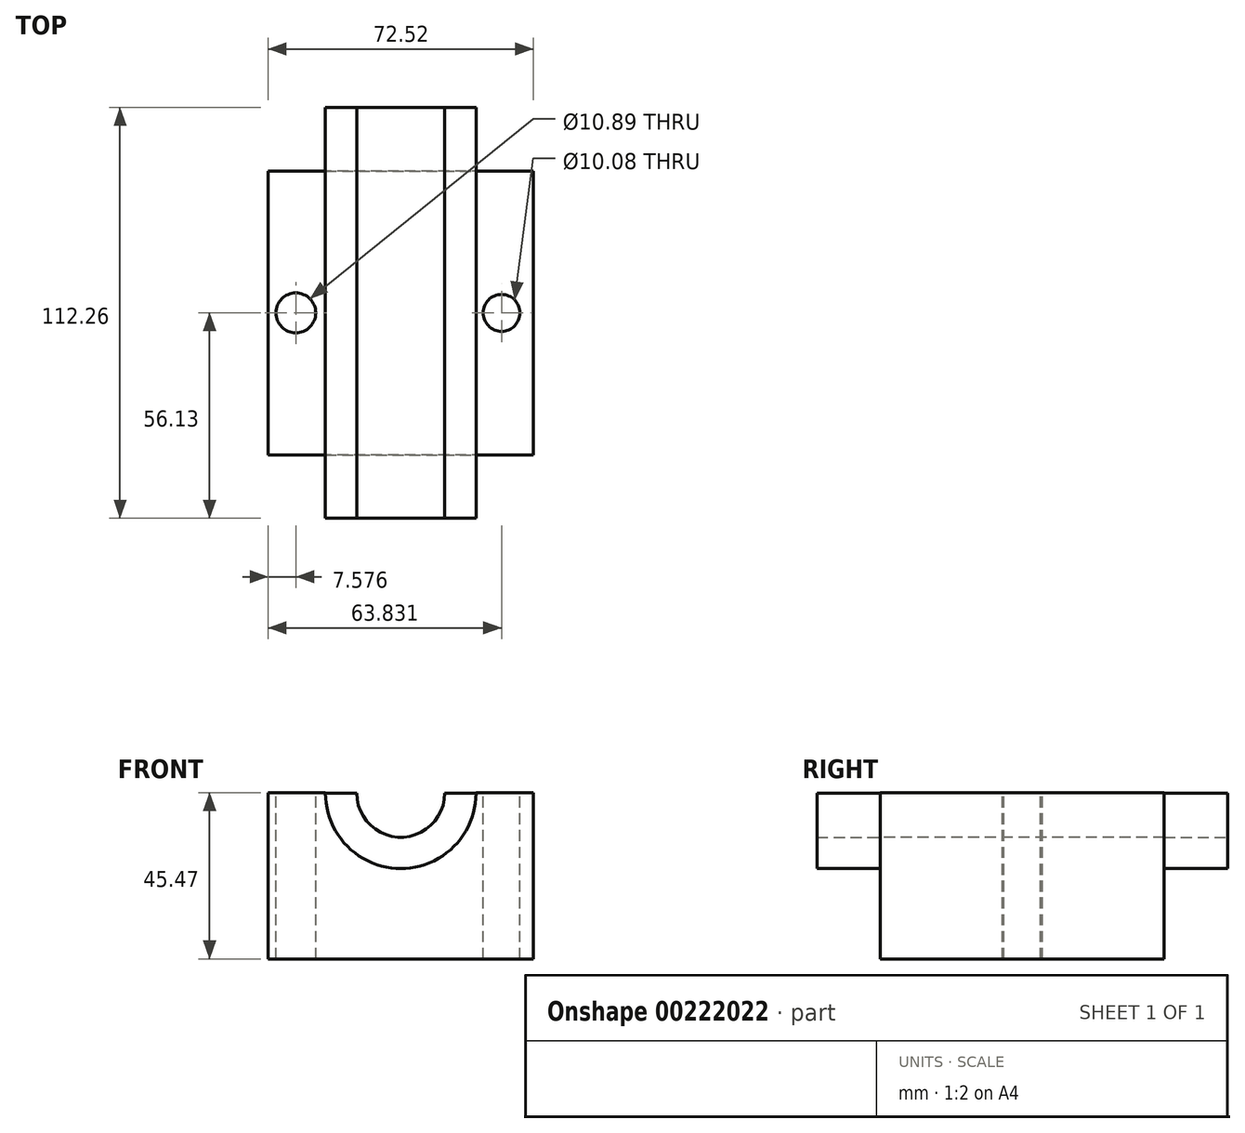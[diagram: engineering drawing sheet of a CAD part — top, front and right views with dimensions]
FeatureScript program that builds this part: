
annotation { "Feature Type Name" : "Feature", "Feature Type Description" : "" }
export const myFeature = defineFeature(function(context is Context, id is Id, definition is map)
    precondition{}
    {
        {
            var Q0;
            Q0=qCreatedBy(makeId("Top.planeOp"),FACE);
            var sketch = newSketch(context, id + "F0", { "sketchPlane" : qUnion([Q0])});
            skLineSegment(sketch, "E0.bottom", {"start": v(36.26, -38.8) * mm, "end": v(-36.26, -38.8) * mm});
            skLineSegment(sketch, "E0.top", {"start": v(36.26, 38.8) * mm, "end": v(-36.26, 38.8) * mm});
            skLineSegment(sketch, "E0.left", {"start": v(36.26, -38.8) * mm, "end": v(36.26, 38.8) * mm});
            skLineSegment(sketch, "E0.right", {"start": v(-36.26, -38.8) * mm, "end": v(-36.26, 38.8) * mm});
            skPoint(sketch, "E0.middle", {"position": v(0, 0) * mm});
            skSolve(sketch);
        }
        {
            var Q0;
            Q0 = qSketchRegion(id + "F0", true);
            extrude(context, id + "F1", {"entities" : qUnion([Q0]), "depth" : 45.47 * mm});
        }
        {
            var Q0;
            Q0=qCreatedBy(makeId("Front.planeOp"),FACE);
            var sketch = newSketch(context, id + "F2", { "sketchPlane" : qUnion([Q0])});
            skCircle(sketch, "E1", {"center": v(0, 45.28) * mm, "radius": 20.59 * mm});
            skCircle(sketch, "E2", {"center": v(0, 45.28) * mm, "radius": 12.02 * mm});
            skSolve(sketch);
        }
        {
            var Q0;
            Q0 = qSketchRegion(id + "F2", true);
            extrude(context, id + "F3", {"entities" : qUnion([Q0]), "operationType" : NewBodyOperationType.ADD, "endBound" : BoundingType.SYMMETRIC, "depth" : 112.27 * mm});
        }
        {
            var Q0;
            Q0=makeQuery(id+"F3.opExtrude","CAP_FACE",FACE,{"disambiguationData":[OSD([sQuery(id+"F2.wireOp",EDGE,"E1"),sQuery(id+"F2.wireOp",EDGE,"E2")])],"isStart":false});
            var sketch = newSketch(context, id + "F4", { "sketchPlane" : qUnion([Q0])});
            skCircle(sketch, "E3", {"center": v(0, 45.28) * mm, "radius": 12.02 * mm});
            skSolve(sketch);
        }
        {
            var Q0;
            Q0 = qSketchRegion(id + "F4", true);
            extrude(context, id + "F5", {"entities" : qUnion([Q0]), "operationType" : NewBodyOperationType.REMOVE, "endBound" : BoundingType.THROUGH_ALL, "oppositeDirection" : true, "depth" : 25.4 * mm});
        }
        {
            var Q0;
            Q0=makeQuery(id+"F3.opExtrude","CAP_FACE",FACE,{"disambiguationData":[OSD([sQuery(id+"F2.wireOp",EDGE,"E1"),sQuery(id+"F2.wireOp",EDGE,"E2")])],"isStart":false});
            var sketch = newSketch(context, id + "F6", { "sketchPlane" : qUnion([Q0])});
            skArc(sketch, "E4", {"start": v(-20.59, 45.3) * mm, "mid": v(0, 65.87) * mm, "end": v(20.59, 45.28) * mm});
            skLineSegment(sketch, "E5", {"start": v(-20.59, 45.3) * mm, "end": v(20.59, 45.28) * mm});
            skSolve(sketch);
        }
        {
            var Q0;
            Q0 = qSketchRegion(id + "F6", true);
            extrude(context, id + "F7", {"entities" : qUnion([Q0]), "operationType" : NewBodyOperationType.REMOVE, "endBound" : BoundingType.THROUGH_ALL, "oppositeDirection" : true, "depth" : 25.4 * mm});
        }
        {
            var Q0;
            {var subQ0=sQuery(id+"F0.wireOp",EDGE,"E0.bottom");var subQ1=sQuery(id+"F0.wireOp",EDGE,"E0.top");var subQ2=sQuery(id+"F0.wireOp",EDGE,"E0.right");Q0=makeQuery(id+"F3.boolean.opBoolean","SPLIT",FACE,{"disambiguationData":[TD([makeQuery(id+"F1.opExtrude","SWEPT_FACE",FACE,{"disambiguationData":[OSD([subQ2])]})])],"derivedFrom":makeQuery(id+"F1.opExtrude","CAP_FACE",FACE,{"disambiguationData":[OSD([subQ0,subQ1,sQuery(id+"F0.wireOp",EDGE,"E0.left"),subQ2])],"isStart":false})});}
            var sketch = newSketch(context, id + "F8", { "sketchPlane" : qUnion([Q0])});
            skCircle(sketch, "E6", {"center": v(-28.68, 0) * mm, "radius": 5.45 * mm});
            skCircle(sketch, "E7", {"center": v(27.57, 0) * mm, "radius": 5.04 * mm});
            skSolve(sketch);
        }
        {
            var Q0;
            Q0 = qSketchRegion(id + "F8", true);
            extrude(context, id + "F9", {"entities" : qUnion([Q0]), "operationType" : NewBodyOperationType.REMOVE, "endBound" : BoundingType.THROUGH_ALL, "oppositeDirection" : true, "depth" : 25.4 * mm});
        }
    });
